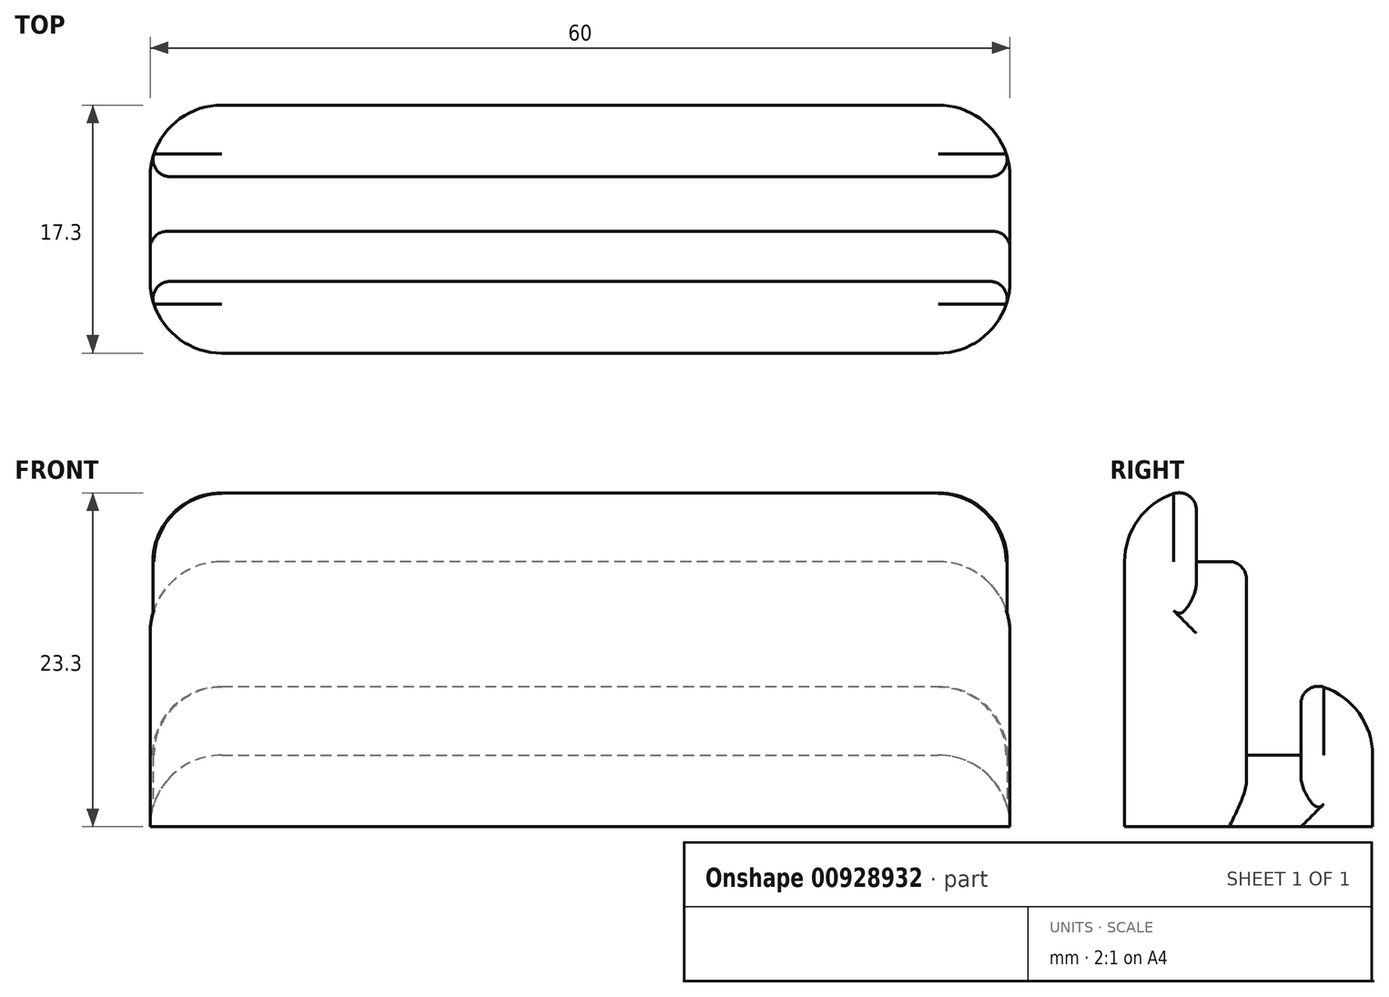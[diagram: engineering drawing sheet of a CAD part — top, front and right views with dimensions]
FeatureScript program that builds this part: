
annotation { "Feature Type Name" : "Feature", "Feature Type Description" : "" }
export const myFeature = defineFeature(function(context is Context, id is Id, definition is map)
    precondition{}
    {
        {
            var Q0;
            Q0=qCreatedBy(makeId("Top.planeOp"),FACE);
            var sketch = newSketch(context, id + "F0", { "sketchPlane" : qUnion([Q0])});
            skLineSegment(sketch, "E0", {"start": v(-8.68, 3.8) * mm, "end": v(51.32, 3.8) * mm});
            skLineSegment(sketch, "E1", {"start": v(51.32, 3.8) * mm, "end": v(51.32, 0) * mm});
            skLineSegment(sketch, "E2", {"start": v(-8.68, 8.8) * mm, "end": v(51.32, 8.8) * mm});
            skLineSegment(sketch, "E3", {"start": v(51.32, 8.8) * mm, "end": v(51.32, 3.8) * mm});
            skLineSegment(sketch, "E4", {"start": v(51.32, 0) * mm, "end": v(51.32, -3.5) * mm});
            skLineSegment(sketch, "E5", {"start": v(51.32, -3.5) * mm, "end": v(51.32, -8.5) * mm});
            skLineSegment(sketch, "E6", {"start": v(51.32, -8.5) * mm, "end": v(-8.68, -8.5) * mm});
            skLineSegment(sketch, "E7", {"start": v(-8.68, -8.5) * mm, "end": v(-8.68, -3.5) * mm});
            skLineSegment(sketch, "E8", {"start": v(-8.68, -3.5) * mm, "end": v(-8.68, 0) * mm});
            skLineSegment(sketch, "E9", {"start": v(-8.68, 0) * mm, "end": v(-8.68, 3.8) * mm});
            skLineSegment(sketch, "E10", {"start": v(-8.68, 3.8) * mm, "end": v(-8.68, 8.8) * mm});
            skLineSegment(sketch, "E11", {"start": v(-8.68, 0) * mm, "end": v(51.32, 0) * mm});
            skLineSegment(sketch, "E12", {"start": v(-8.68, -3.5) * mm, "end": v(51.32, -3.5) * mm});
            skSolve(sketch);
        }
        {
            var Q0;
            Q0=makeQuery(id+"F0.imprint","IMPRINT",FACE,{"disambiguationData":[TD([[makeQuery(id+"F0.imprint","IMPRINT",EDGE,{"derivedFrom":sQuery(id+"F0.wireOp",EDGE,"E0")}),1.0]])]});
            var Q1;
            Q1=makeQuery(id+"F0.imprint","IMPRINT",FACE,{"disambiguationData":[TD([[makeQuery(id+"F0.imprint","IMPRINT",EDGE,{"derivedFrom":sQuery(id+"F0.wireOp",EDGE,"E0")}),-1.0]])]});
            var Q2;
            Q2=makeQuery(id+"F0.imprint","IMPRINT",FACE,{"disambiguationData":[TD([[makeQuery(id+"F0.imprint","IMPRINT",EDGE,{"derivedFrom":sQuery(id+"F0.wireOp",EDGE,"E4")}),-1.0]])]});
            var Q3;
            Q3=makeQuery(id+"F0.imprint","IMPRINT",FACE,{"disambiguationData":[TD([[makeQuery(id+"F0.imprint","IMPRINT",EDGE,{"derivedFrom":sQuery(id+"F0.wireOp",EDGE,"E5")}),-1.0]])]});
            extrude(context, id + "F1", {"entities" : qUnion([Q0, Q1, Q2, Q3]), "depth" : 5 * mm, "offsetDistance" : 25 * mm});
        }
        {
            var Q0;
            Q0=makeQuery(id+"F1.opExtrude","CAP_FACE",FACE,{"disambiguationData":[OSD([sQuery(id+"F0.wireOp",EDGE,"E1"),sQuery(id+"F0.wireOp",EDGE,"E2"),sQuery(id+"F0.wireOp",EDGE,"E3"),sQuery(id+"F0.wireOp",EDGE,"E4"),sQuery(id+"F0.wireOp",EDGE,"E5"),sQuery(id+"F0.wireOp",EDGE,"E6"),sQuery(id+"F0.wireOp",EDGE,"E7"),sQuery(id+"F0.wireOp",EDGE,"E8"),sQuery(id+"F0.wireOp",EDGE,"E9"),sQuery(id+"F0.wireOp",EDGE,"E10")])],"isStart":false});
            var sketch = newSketch(context, id + "F2", { "sketchPlane" : qUnion([Q0])});
            skLineSegment(sketch, "E13", {"start": v(-8.68, 3.8) * mm, "end": v(51.32, 3.8) * mm});
            skLineSegment(sketch, "E14", {"start": v(51.32, 3.8) * mm, "end": v(51.32, 0) * mm});
            skLineSegment(sketch, "E15", {"start": v(51.32, 0) * mm, "end": v(-8.68, 0) * mm});
            skLineSegment(sketch, "E16", {"start": v(-8.68, 8.8) * mm, "end": v(51.32, 8.8) * mm});
            skLineSegment(sketch, "E17", {"start": v(51.32, 8.8) * mm, "end": v(51.32, 3.8) * mm});
            skLineSegment(sketch, "E18", {"start": v(51.32, 0) * mm, "end": v(51.32, -3.5) * mm});
            skLineSegment(sketch, "E19", {"start": v(51.32, -3.5) * mm, "end": v(51.32, -8.5) * mm});
            skLineSegment(sketch, "E20", {"start": v(51.32, -8.5) * mm, "end": v(-8.68, -8.5) * mm});
            skLineSegment(sketch, "E21", {"start": v(-8.68, -3.5) * mm, "end": v(51.32, -3.5) * mm});
            skLineSegment(sketch, "E22", {"start": v(-8.68, 8.8) * mm, "end": v(-8.68, 3.8) * mm});
            skLineSegment(sketch, "E23", {"start": v(-8.68, 3.8) * mm, "end": v(-8.68, 0) * mm});
            skLineSegment(sketch, "E24", {"start": v(-8.68, 0) * mm, "end": v(-8.68, -3.5) * mm});
            skLineSegment(sketch, "E25", {"start": v(-8.68, -3.5) * mm, "end": v(-8.68, -8.5) * mm});
            skSolve(sketch);
        }
        {
            var Q0;
            Q0=makeQuery(id+"F2.imprint","IMPRINT",FACE,{"disambiguationData":[TD([[makeQuery(id+"F2.imprint","IMPRINT",EDGE,{"derivedFrom":sQuery(id+"F2.wireOp",EDGE,"E13")}),1.0]])]});
            var Q1;
            Q1=makeQuery(id+"F2.imprint","IMPRINT",FACE,{"disambiguationData":[TD([[makeQuery(id+"F2.imprint","IMPRINT",EDGE,{"derivedFrom":sQuery(id+"F2.wireOp",EDGE,"E15")}),1.0]])]});
            var Q2;
            Q2=makeQuery(id+"F2.imprint","IMPRINT",FACE,{"disambiguationData":[TD([[makeQuery(id+"F2.imprint","IMPRINT",EDGE,{"derivedFrom":sQuery(id+"F2.wireOp",EDGE,"E19")}),-1.0]])]});
            extrude(context, id + "F3", {"entities" : qUnion([Q0, Q1, Q2]), "operationType" : NewBodyOperationType.ADD, "depth" : 5 * mm, "offsetDistance" : 25 * mm});
        }
        {
            var Q0;
            Q0=makeQuery(id+"F3.opExtrude","CAP_FACE",FACE,{"disambiguationData":[OSD([sQuery(id+"F2.wireOp",EDGE,"E15"),sQuery(id+"F2.wireOp",EDGE,"E18"),sQuery(id+"F2.wireOp",EDGE,"E19"),sQuery(id+"F2.wireOp",EDGE,"E20"),sQuery(id+"F2.wireOp",EDGE,"E24"),sQuery(id+"F2.wireOp",EDGE,"E25")])],"isStart":false});
            var sketch = newSketch(context, id + "F4", { "sketchPlane" : qUnion([Q0])});
            skLineSegment(sketch, "E26", {"start": v(-8.68, 3.6) * mm, "end": v(51.32, 3.6) * mm});
            skLineSegment(sketch, "E27", {"start": v(51.32, 3.6) * mm, "end": v(51.32, 0) * mm});
            skLineSegment(sketch, "E28", {"start": v(51.32, 0) * mm, "end": v(-8.68, 0) * mm});
            skLineSegment(sketch, "E29", {"start": v(-8.68, 8.6) * mm, "end": v(51.32, 8.6) * mm});
            skLineSegment(sketch, "E30", {"start": v(51.32, 8.6) * mm, "end": v(51.32, 3.6) * mm});
            skLineSegment(sketch, "E31", {"start": v(51.32, 0) * mm, "end": v(51.32, -3.5) * mm});
            skLineSegment(sketch, "E32", {"start": v(51.32, -3.5) * mm, "end": v(51.32, -8.5) * mm});
            skLineSegment(sketch, "E33", {"start": v(51.32, -8.5) * mm, "end": v(-8.68, -8.5) * mm});
            skLineSegment(sketch, "E34", {"start": v(-8.68, -3.5) * mm, "end": v(51.32, -3.5) * mm});
            skLineSegment(sketch, "E35", {"start": v(-8.68, 8.6) * mm, "end": v(-8.68, 3.6) * mm});
            skLineSegment(sketch, "E36", {"start": v(-8.68, 3.6) * mm, "end": v(-8.68, 0) * mm});
            skLineSegment(sketch, "E37", {"start": v(-8.68, 0) * mm, "end": v(-8.68, -3.5) * mm});
            skLineSegment(sketch, "E38", {"start": v(-8.68, -3.5) * mm, "end": v(-8.68, -8.5) * mm});
            skSolve(sketch);
        }
        {
            var Q0;
            Q0=makeQuery(id+"F4.imprint","IMPRINT",FACE,{"disambiguationData":[TD([[makeQuery(id+"F4.imprint","IMPRINT",EDGE,{"derivedFrom":sQuery(id+"F4.wireOp",EDGE,"E32")}),-1.0]])]});
            var Q1;
            Q1=makeQuery(id+"F4.imprint","IMPRINT",FACE,{"disambiguationData":[TD([[makeQuery(id+"F4.imprint","IMPRINT",EDGE,{"derivedFrom":sQuery(id+"F4.wireOp",EDGE,"E28")}),1.0]])]});
            extrude(context, id + "F5", {"entities" : qUnion([Q0, Q1]), "operationType" : NewBodyOperationType.ADD, "depth" : 8.5 * mm, "offsetDistance" : 25 * mm});
        }
        {
            var Q0;
            Q0=makeQuery(id+"F5.opExtrude","CAP_FACE",FACE,{"disambiguationData":[OSD([sQuery(id+"F4.wireOp",EDGE,"E28"),sQuery(id+"F4.wireOp",EDGE,"E31"),sQuery(id+"F4.wireOp",EDGE,"E32"),sQuery(id+"F4.wireOp",EDGE,"E33"),sQuery(id+"F4.wireOp",EDGE,"E37"),sQuery(id+"F4.wireOp",EDGE,"E38")])],"isStart":false});
            var sketch = newSketch(context, id + "F6", { "sketchPlane" : qUnion([Q0])});
            skLineSegment(sketch, "E39", {"start": v(-8.68, 3.6) * mm, "end": v(51.32, 3.6) * mm});
            skLineSegment(sketch, "E40", {"start": v(51.32, 3.6) * mm, "end": v(51.32, 0) * mm});
            skLineSegment(sketch, "E41", {"start": v(51.32, 0) * mm, "end": v(-8.68, 0) * mm});
            skLineSegment(sketch, "E42", {"start": v(-8.68, 8.6) * mm, "end": v(51.32, 8.6) * mm});
            skLineSegment(sketch, "E43", {"start": v(51.32, 8.6) * mm, "end": v(51.32, 3.6) * mm});
            skLineSegment(sketch, "E44", {"start": v(51.32, 0) * mm, "end": v(51.32, -3.5) * mm});
            skLineSegment(sketch, "E45", {"start": v(51.32, -3.5) * mm, "end": v(51.32, -8.5) * mm});
            skLineSegment(sketch, "E46", {"start": v(51.32, -8.5) * mm, "end": v(-8.68, -8.5) * mm});
            skLineSegment(sketch, "E47", {"start": v(-8.68, -3.5) * mm, "end": v(51.32, -3.5) * mm});
            skLineSegment(sketch, "E48", {"start": v(-8.68, 8.6) * mm, "end": v(-8.68, 3.6) * mm});
            skLineSegment(sketch, "E49", {"start": v(-8.68, 3.6) * mm, "end": v(-8.68, 0) * mm});
            skLineSegment(sketch, "E50", {"start": v(-8.68, 0) * mm, "end": v(-8.68, -3.5) * mm});
            skLineSegment(sketch, "E51", {"start": v(-8.68, -3.5) * mm, "end": v(-8.68, -8.5) * mm});
            skSolve(sketch);
        }
        {
            var Q0;
            Q0=makeQuery(id+"F6.imprint","IMPRINT",FACE,{"disambiguationData":[TD([[makeQuery(id+"F6.imprint","IMPRINT",EDGE,{"derivedFrom":sQuery(id+"F6.wireOp",EDGE,"E45")}),-1.0]])]});
            extrude(context, id + "F7", {"entities" : qUnion([Q0]), "operationType" : NewBodyOperationType.ADD, "depth" : 5 * mm, "offsetDistance" : 25 * mm});
        }
        {
            var Q0;
            Q0=makeQuery(id+"F3.opExtrude","CAP_EDGE",EDGE,{"disambiguationData":[OSD([sQuery(id+"F2.wireOp",EDGE,"E16")])],"isStart":false});
            var Q1;
            Q1=makeQuery(id+"F7.boolean.opBoolean","MERGE",EDGE,{"derivedFrom":[makeQuery(id+"F5.boolean.opBoolean","MERGE",EDGE,{"derivedFrom":[makeQuery(id+"F3.boolean.opBoolean","MERGE",EDGE,{"derivedFrom":[makeQuery(id+"F1.opExtrude","SWEPT_EDGE",EDGE,{"disambiguationData":[OSD([sQuery(id+"F0.wireOp",EDGE,"E6"),sQuery(id+"F0.wireOp",EDGE,"E7")])]}),makeQuery(id+"F3.opExtrude","SWEPT_EDGE",EDGE,{"disambiguationData":[OSD([sQuery(id+"F2.wireOp",EDGE,"E20"),sQuery(id+"F2.wireOp",EDGE,"E25")])]})]}),makeQuery(id+"F5.opExtrude","SWEPT_EDGE",EDGE,{"disambiguationData":[OSD([sQuery(id+"F4.wireOp",EDGE,"E33"),sQuery(id+"F4.wireOp",EDGE,"E38")])]})]}),makeQuery(id+"F7.opExtrude","SWEPT_EDGE",EDGE,{"disambiguationData":[OSD([sQuery(id+"F6.wireOp",EDGE,"E46"),sQuery(id+"F6.wireOp",EDGE,"E51")])]})]});
            var Q2;
            Q2=makeQuery(id+"F3.boolean.opBoolean","MERGE",EDGE,{"derivedFrom":[makeQuery(id+"F1.opExtrude","SWEPT_EDGE",EDGE,{"disambiguationData":[OSD([sQuery(id+"F0.wireOp",EDGE,"E2"),sQuery(id+"F0.wireOp",EDGE,"E10")])]}),makeQuery(id+"F3.opExtrude","SWEPT_EDGE",EDGE,{"disambiguationData":[OSD([sQuery(id+"F2.wireOp",EDGE,"E16"),sQuery(id+"F2.wireOp",EDGE,"E22")])]})]});
            var Q3;
            Q3=makeQuery(id+"F3.boolean.opBoolean","MERGE",EDGE,{"derivedFrom":[makeQuery(id+"F1.opExtrude","SWEPT_EDGE",EDGE,{"disambiguationData":[OSD([sQuery(id+"F0.wireOp",EDGE,"E2"),sQuery(id+"F0.wireOp",EDGE,"E3")])]}),makeQuery(id+"F3.opExtrude","SWEPT_EDGE",EDGE,{"disambiguationData":[OSD([sQuery(id+"F2.wireOp",EDGE,"E16"),sQuery(id+"F2.wireOp",EDGE,"E17")])]})]});
            var Q4;
            Q4=makeQuery(id+"F7.boolean.opBoolean","MERGE",EDGE,{"derivedFrom":[makeQuery(id+"F5.boolean.opBoolean","MERGE",EDGE,{"derivedFrom":[makeQuery(id+"F3.boolean.opBoolean","MERGE",EDGE,{"derivedFrom":[makeQuery(id+"F1.opExtrude","SWEPT_EDGE",EDGE,{"disambiguationData":[OSD([sQuery(id+"F0.wireOp",EDGE,"E5"),sQuery(id+"F0.wireOp",EDGE,"E6")])]}),makeQuery(id+"F3.opExtrude","SWEPT_EDGE",EDGE,{"disambiguationData":[OSD([sQuery(id+"F2.wireOp",EDGE,"E19"),sQuery(id+"F2.wireOp",EDGE,"E20")])]})]}),makeQuery(id+"F5.opExtrude","SWEPT_EDGE",EDGE,{"disambiguationData":[OSD([sQuery(id+"F4.wireOp",EDGE,"E32"),sQuery(id+"F4.wireOp",EDGE,"E33")])]})]}),makeQuery(id+"F7.opExtrude","SWEPT_EDGE",EDGE,{"disambiguationData":[OSD([sQuery(id+"F6.wireOp",EDGE,"E45"),sQuery(id+"F6.wireOp",EDGE,"E46")])]})]});
            fillet(context, id + "F8", {"entities" : qUnion([Q0, Q1, Q2, Q3, Q4]), "radius" : 5 * mm, "tangentPropagation" : true, "allowEdgeOverflow" : false});
        }
        {
            var Q0;
            Q0=makeQuery(id+"F1.opExtrude","CAP_EDGE",EDGE,{"disambiguationData":[OSD([sQuery(id+"F0.wireOp",EDGE,"E1"),sQuery(id+"F0.wireOp",EDGE,"E3"),sQuery(id+"F0.wireOp",EDGE,"E4"),sQuery(id+"F0.wireOp",EDGE,"E5")])],"isStart":false});
            var Q1;
            Q1=makeQuery(id+"F1.opExtrude","CAP_EDGE",EDGE,{"disambiguationData":[OSD([sQuery(id+"F0.wireOp",EDGE,"E7"),sQuery(id+"F0.wireOp",EDGE,"E8"),sQuery(id+"F0.wireOp",EDGE,"E9"),sQuery(id+"F0.wireOp",EDGE,"E10")])],"isStart":false});
            var Q2;
            Q2=makeQuery(id+"F5.opExtrude","CAP_EDGE",EDGE,{"disambiguationData":[OSD([sQuery(id+"F4.wireOp",EDGE,"E37"),sQuery(id+"F4.wireOp",EDGE,"E38")])],"isStart":false});
            var Q3;
            Q3=makeQuery(id+"F5.opExtrude","CAP_EDGE",EDGE,{"disambiguationData":[OSD([sQuery(id+"F4.wireOp",EDGE,"E31"),sQuery(id+"F4.wireOp",EDGE,"E32")])],"isStart":false});
            var Q4;
            Q4=makeQuery(id+"F7.opExtrude","CAP_EDGE",EDGE,{"disambiguationData":[OSD([sQuery(id+"F6.wireOp",EDGE,"E46")])],"isStart":false});
            fillet(context, id + "F9", {"entities" : qUnion([Q0, Q1, Q2, Q3, Q4]), "radius" : 5 * mm, "tangentPropagation" : true, "allowEdgeOverflow" : false});
        }
        {
            var Q0;
            Q0=makeQuery(id+"F5.boolean.opBoolean","MERGE",EDGE,{"derivedFrom":[makeQuery(id+"F3.opExtrude","SWEPT_EDGE",EDGE,{"disambiguationData":[OSD([sQuery(id+"F2.wireOp",EDGE,"E15"),sQuery(id+"F2.wireOp",EDGE,"E23"),sQuery(id+"F2.wireOp",EDGE,"E24")])]}),makeQuery(id+"F5.opExtrude","SWEPT_EDGE",EDGE,{"disambiguationData":[OSD([sQuery(id+"F4.wireOp",EDGE,"E28"),sQuery(id+"F4.wireOp",EDGE,"E36"),sQuery(id+"F4.wireOp",EDGE,"E37")])]})]});
            var Q1;
            Q1=makeQuery(id+"F9.opFillet","BLEND_EDGE",EDGE,{"blendedFrom":[makeQuery(id+"F7.opExtrude","CAP_EDGE",EDGE,{"disambiguationData":[OSD([sQuery(id+"F6.wireOp",EDGE,"E46")])],"isStart":false}),makeQuery(id+"F7.opExtrude","SWEPT_FACE",FACE,{"disambiguationData":[OSD([sQuery(id+"F6.wireOp",EDGE,"E47")])]})],"blendedInto":[makeQuery(id+"F7.opExtrude","SWEPT_FACE",FACE,{"disambiguationData":[OSD([sQuery(id+"F6.wireOp",EDGE,"E47")])]})]});
            var Q2;
            Q2=makeQuery(id+"F8.opFillet","BLEND_EDGE",EDGE,{"blendedFrom":[makeQuery(id+"F3.opExtrude","CAP_EDGE",EDGE,{"disambiguationData":[OSD([sQuery(id+"F2.wireOp",EDGE,"E16")])],"isStart":false}),makeQuery(id+"F3.opExtrude","SWEPT_FACE",FACE,{"disambiguationData":[OSD([sQuery(id+"F2.wireOp",EDGE,"E13")])]})],"blendedInto":[makeQuery(id+"F3.opExtrude","SWEPT_FACE",FACE,{"disambiguationData":[OSD([sQuery(id+"F2.wireOp",EDGE,"E13")])]})]});
            var Q3;
            {var subQ0=sQuery(id+"F2.wireOp",EDGE,"E22");var subQ1=sQuery(id+"F0.wireOp",EDGE,"E10");var subQ2=makeQuery(id+"F3.boolean.opBoolean","MERGE",EDGE,{"derivedFrom":[makeQuery(id+"F1.opExtrude","SWEPT_EDGE",EDGE,{"disambiguationData":[OSD([sQuery(id+"F0.wireOp",EDGE,"E2"),subQ1])]}),makeQuery(id+"F3.opExtrude","SWEPT_EDGE",EDGE,{"disambiguationData":[OSD([sQuery(id+"F2.wireOp",EDGE,"E16"),subQ0])]})]});Q3=makeQuery(id+"F9.opFillet","MERGE",EDGE,{"derivedFrom":[makeQuery(id+"F8.opFillet","BLEND_EDGE",EDGE,{"blendedFrom":[subQ2,makeQuery(id+"F3.opExtrude","SWEPT_FACE",FACE,{"disambiguationData":[OSD([sQuery(id+"F2.wireOp",EDGE,"E13")])]})],"blendedInto":[makeQuery(id+"F3.opExtrude","SWEPT_FACE",FACE,{"disambiguationData":[OSD([sQuery(id+"F2.wireOp",EDGE,"E13")])]})]}),makeQuery(id+"F8.opFillet","BLEND_EDGE",EDGE,{"blendedFrom":[subQ2,makeQuery(id+"F7.boolean.opBoolean","MERGE",FACE,{"derivedFrom":[makeQuery(id+"F5.boolean.opBoolean","MERGE",FACE,{"derivedFrom":[makeQuery(id+"F3.boolean.opBoolean","MERGE",FACE,{"derivedFrom":[makeQuery(id+"F1.opExtrude","SWEPT_FACE",FACE,{"disambiguationData":[OSD([sQuery(id+"F0.wireOp",EDGE,"E7"),sQuery(id+"F0.wireOp",EDGE,"E8"),sQuery(id+"F0.wireOp",EDGE,"E9"),subQ1])]}),makeQuery(id+"F3.opExtrude","SWEPT_FACE",FACE,{"disambiguationData":[OSD([subQ0])]}),makeQuery(id+"F3.opExtrude","SWEPT_FACE",FACE,{"disambiguationData":[OSD([sQuery(id+"F2.wireOp",EDGE,"E24"),sQuery(id+"F2.wireOp",EDGE,"E25")])]})]}),makeQuery(id+"F5.opExtrude","SWEPT_FACE",FACE,{"disambiguationData":[OSD([sQuery(id+"F4.wireOp",EDGE,"E37"),sQuery(id+"F4.wireOp",EDGE,"E38")])]})]}),makeQuery(id+"F7.opExtrude","SWEPT_FACE",FACE,{"disambiguationData":[OSD([sQuery(id+"F6.wireOp",EDGE,"E51")])]})]})],"blendedInto":[makeQuery(id+"F7.boolean.opBoolean","MERGE",FACE,{"derivedFrom":[makeQuery(id+"F5.boolean.opBoolean","MERGE",FACE,{"derivedFrom":[makeQuery(id+"F3.boolean.opBoolean","MERGE",FACE,{"derivedFrom":[makeQuery(id+"F1.opExtrude","SWEPT_FACE",FACE,{"disambiguationData":[OSD([sQuery(id+"F0.wireOp",EDGE,"E7"),sQuery(id+"F0.wireOp",EDGE,"E8"),sQuery(id+"F0.wireOp",EDGE,"E9"),subQ1])]}),makeQuery(id+"F3.opExtrude","SWEPT_FACE",FACE,{"disambiguationData":[OSD([subQ0])]}),makeQuery(id+"F3.opExtrude","SWEPT_FACE",FACE,{"disambiguationData":[OSD([sQuery(id+"F2.wireOp",EDGE,"E24"),sQuery(id+"F2.wireOp",EDGE,"E25")])]})]}),makeQuery(id+"F5.opExtrude","SWEPT_FACE",FACE,{"disambiguationData":[OSD([sQuery(id+"F4.wireOp",EDGE,"E37"),sQuery(id+"F4.wireOp",EDGE,"E38")])]})]}),makeQuery(id+"F7.opExtrude","SWEPT_FACE",FACE,{"disambiguationData":[OSD([sQuery(id+"F6.wireOp",EDGE,"E51")])]})]})]})]});}
            var Q4;
            {var subQ0=sQuery(id+"F2.wireOp",EDGE,"E17");var subQ1=sQuery(id+"F0.wireOp",EDGE,"E3");var subQ2=makeQuery(id+"F3.boolean.opBoolean","MERGE",EDGE,{"derivedFrom":[makeQuery(id+"F1.opExtrude","SWEPT_EDGE",EDGE,{"disambiguationData":[OSD([sQuery(id+"F0.wireOp",EDGE,"E2"),subQ1])]}),makeQuery(id+"F3.opExtrude","SWEPT_EDGE",EDGE,{"disambiguationData":[OSD([sQuery(id+"F2.wireOp",EDGE,"E16"),subQ0])]})]});Q4=makeQuery(id+"F9.opFillet","MERGE",EDGE,{"derivedFrom":[makeQuery(id+"F8.opFillet","BLEND_EDGE",EDGE,{"blendedFrom":[subQ2,makeQuery(id+"F3.opExtrude","SWEPT_FACE",FACE,{"disambiguationData":[OSD([sQuery(id+"F2.wireOp",EDGE,"E13")])]})],"blendedInto":[makeQuery(id+"F3.opExtrude","SWEPT_FACE",FACE,{"disambiguationData":[OSD([sQuery(id+"F2.wireOp",EDGE,"E13")])]})]}),makeQuery(id+"F8.opFillet","BLEND_EDGE",EDGE,{"blendedFrom":[subQ2,makeQuery(id+"F7.boolean.opBoolean","MERGE",FACE,{"derivedFrom":[makeQuery(id+"F5.boolean.opBoolean","MERGE",FACE,{"derivedFrom":[makeQuery(id+"F3.boolean.opBoolean","MERGE",FACE,{"derivedFrom":[makeQuery(id+"F1.opExtrude","SWEPT_FACE",FACE,{"disambiguationData":[OSD([sQuery(id+"F0.wireOp",EDGE,"E1"),subQ1,sQuery(id+"F0.wireOp",EDGE,"E4"),sQuery(id+"F0.wireOp",EDGE,"E5")])]}),makeQuery(id+"F3.opExtrude","SWEPT_FACE",FACE,{"disambiguationData":[OSD([subQ0])]}),makeQuery(id+"F3.opExtrude","SWEPT_FACE",FACE,{"disambiguationData":[OSD([sQuery(id+"F2.wireOp",EDGE,"E18"),sQuery(id+"F2.wireOp",EDGE,"E19")])]})]}),makeQuery(id+"F5.opExtrude","SWEPT_FACE",FACE,{"disambiguationData":[OSD([sQuery(id+"F4.wireOp",EDGE,"E31"),sQuery(id+"F4.wireOp",EDGE,"E32")])]})]}),makeQuery(id+"F7.opExtrude","SWEPT_FACE",FACE,{"disambiguationData":[OSD([sQuery(id+"F6.wireOp",EDGE,"E45")])]})]})],"blendedInto":[makeQuery(id+"F7.boolean.opBoolean","MERGE",FACE,{"derivedFrom":[makeQuery(id+"F5.boolean.opBoolean","MERGE",FACE,{"derivedFrom":[makeQuery(id+"F3.boolean.opBoolean","MERGE",FACE,{"derivedFrom":[makeQuery(id+"F1.opExtrude","SWEPT_FACE",FACE,{"disambiguationData":[OSD([sQuery(id+"F0.wireOp",EDGE,"E1"),subQ1,sQuery(id+"F0.wireOp",EDGE,"E4"),sQuery(id+"F0.wireOp",EDGE,"E5")])]}),makeQuery(id+"F3.opExtrude","SWEPT_FACE",FACE,{"disambiguationData":[OSD([subQ0])]}),makeQuery(id+"F3.opExtrude","SWEPT_FACE",FACE,{"disambiguationData":[OSD([sQuery(id+"F2.wireOp",EDGE,"E18"),sQuery(id+"F2.wireOp",EDGE,"E19")])]})]}),makeQuery(id+"F5.opExtrude","SWEPT_FACE",FACE,{"disambiguationData":[OSD([sQuery(id+"F4.wireOp",EDGE,"E31"),sQuery(id+"F4.wireOp",EDGE,"E32")])]})]}),makeQuery(id+"F7.opExtrude","SWEPT_FACE",FACE,{"disambiguationData":[OSD([sQuery(id+"F6.wireOp",EDGE,"E45")])]})]})]})]});}
            fillet(context, id + "F10", {"entities" : qUnion([Q0, Q1, Q2, Q3, Q4]), "radius" : 1.2 * mm, "tangentPropagation" : true, "allowEdgeOverflow" : false});
        }
        {
            var Q0;
            {var subQ0=sQuery(id+"F2.wireOp",EDGE,"E16");Q0=makeQuery(id+"F8.opFillet","BLEND_EDGE",EDGE,{"blendedFrom":[makeQuery(id+"F3.opExtrude","CAP_EDGE",EDGE,{"disambiguationData":[OSD([subQ0])],"isStart":false}),makeQuery(id+"F3.boolean.opBoolean","MERGE",EDGE,{"derivedFrom":[makeQuery(id+"F1.opExtrude","SWEPT_EDGE",EDGE,{"disambiguationData":[OSD([sQuery(id+"F0.wireOp",EDGE,"E2"),sQuery(id+"F0.wireOp",EDGE,"E3")])]}),makeQuery(id+"F3.opExtrude","SWEPT_EDGE",EDGE,{"disambiguationData":[OSD([subQ0,sQuery(id+"F2.wireOp",EDGE,"E17")])]})]})],"blendedInto":[]});}
            var Q1;
            {var subQ0=sQuery(id+"F2.wireOp",EDGE,"E16");Q1=makeQuery(id+"F8.opFillet","BLEND_EDGE",EDGE,{"blendedFrom":[makeQuery(id+"F3.opExtrude","CAP_EDGE",EDGE,{"disambiguationData":[OSD([subQ0])],"isStart":false}),makeQuery(id+"F3.boolean.opBoolean","MERGE",EDGE,{"derivedFrom":[makeQuery(id+"F1.opExtrude","SWEPT_EDGE",EDGE,{"disambiguationData":[OSD([sQuery(id+"F0.wireOp",EDGE,"E2"),sQuery(id+"F0.wireOp",EDGE,"E10")])]}),makeQuery(id+"F3.opExtrude","SWEPT_EDGE",EDGE,{"disambiguationData":[OSD([subQ0,sQuery(id+"F2.wireOp",EDGE,"E22")])]})]})],"blendedInto":[]});}
            fillet(context, id + "F11", {"entities" : qUnion([Q0, Q1]), "radius" : 5 * mm, "tangentPropagation" : true, "allowEdgeOverflow" : false});
        }
    });
